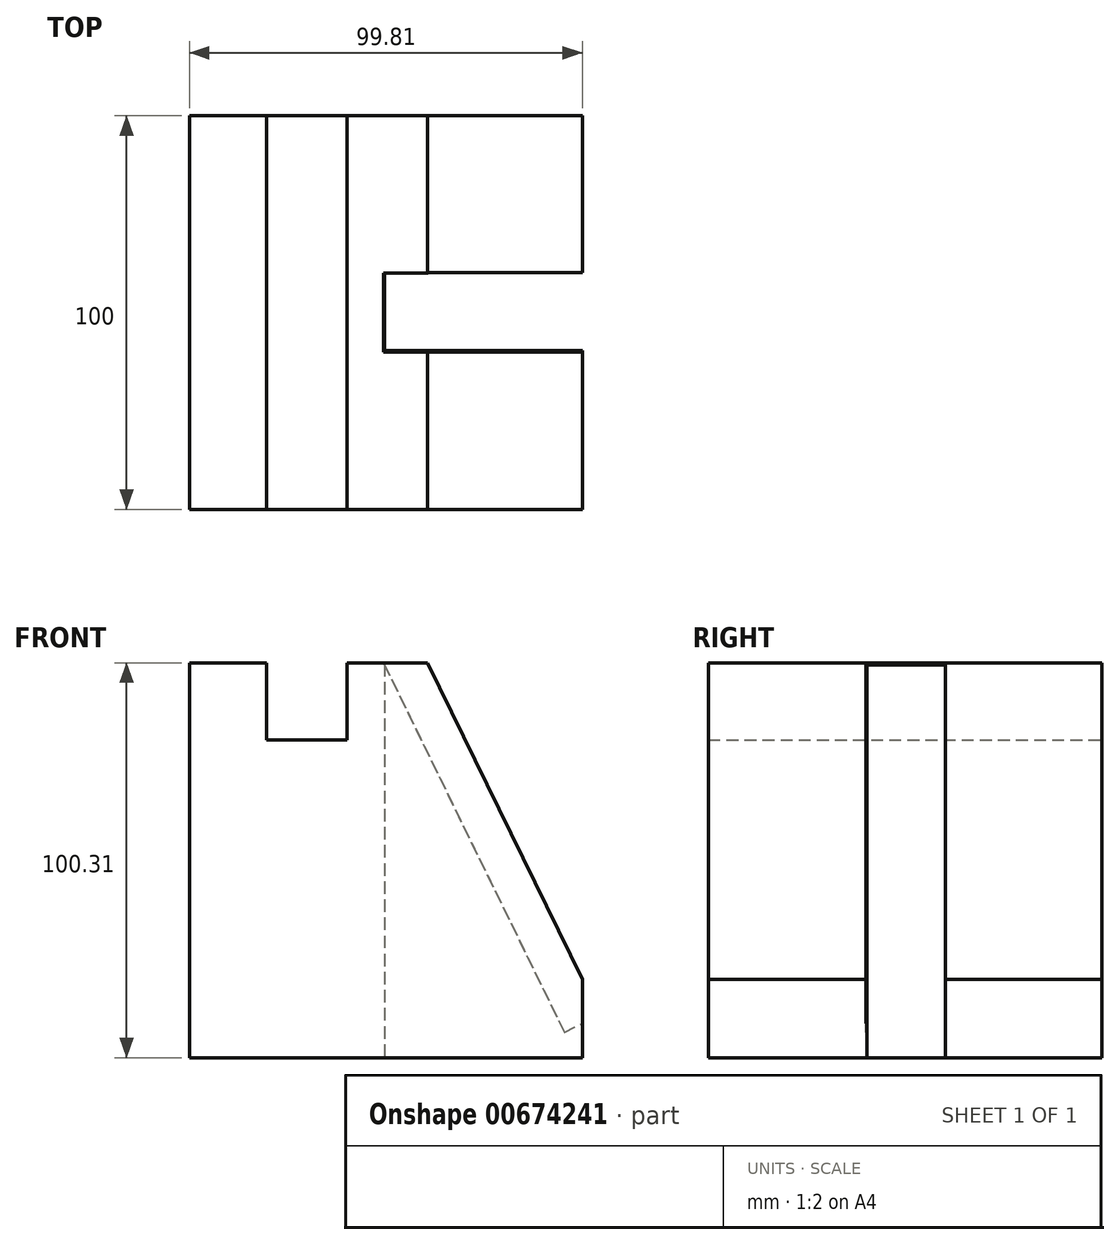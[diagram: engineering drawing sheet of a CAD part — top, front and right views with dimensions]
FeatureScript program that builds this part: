
annotation { "Feature Type Name" : "Feature", "Feature Type Description" : "" }
export const myFeature = defineFeature(function(context is Context, id is Id, definition is map)
    precondition{}
    {
        {
            var Q0;
            Q0=qCreatedBy(makeId("Front.planeOp"),FACE);
            var sketch = newSketch(context, id + "F0", { "sketchPlane" : qUnion([Q0])});
            skLineSegment(sketch, "E0", {"start": v(-74.7, 75.5) * mm, "end": v(-55.16, 75.5) * mm});
            skLineSegment(sketch, "E1", {"start": v(-55.16, 75.5) * mm, "end": v(-55.16, 55.95) * mm});
            skLineSegment(sketch, "E2", {"start": v(-55.16, 55.95) * mm, "end": v(-34.72, 55.95) * mm});
            skLineSegment(sketch, "E3", {"start": v(-34.72, 55.95) * mm, "end": v(-34.72, 75.5) * mm});
            skLineSegment(sketch, "E4", {"start": v(-34.72, 75.5) * mm, "end": v(-14.28, 75.5) * mm});
            skLineSegment(sketch, "E5", {"start": v(-74.7, 75.5) * mm, "end": v(-74.7, -24.82) * mm});
            skLineSegment(sketch, "E6", {"start": v(-74.7, -24.82) * mm, "end": v(25.11, -24.82) * mm});
            skLineSegment(sketch, "E7", {"start": v(25.11, -24.82) * mm, "end": v(25.11, -4.99) * mm});
            skLineSegment(sketch, "E8", {"start": v(25.11, -4.99) * mm, "end": v(-14.28, 75.5) * mm});
            skSolve(sketch);
        }
        {
            var Q0;
            Q0=makeQuery(id+"F0.imprint","IMPRINT",FACE,{"disambiguationData":[TD([[makeQuery(id+"F0.imprint","IMPRINT",EDGE,{"derivedFrom":sQuery(id+"F0.wireOp",EDGE,"E0")}),-1.0]])]});
            extrude(context, id + "F1", {"entities" : qUnion([Q0]), "depth" : 100 * mm, "offsetDistance" : 25 * mm});
        }
        {
            var Q0;
            Q0=makeQuery(id+"F1.opExtrude","SWEPT_FACE",FACE,{"disambiguationData":[OSD([sQuery(id+"F0.wireOp",EDGE,"E8")])]});
            var sketch = newSketch(context, id + "F2", { "sketchPlane" : qUnion([Q0])});
            skLineSegment(sketch, "E9", {"start": v(-100, 74.09) * mm, "end": v(-60, 74.09) * mm});
            skLineSegment(sketch, "E10", {"start": v(-60, 74.09) * mm, "end": v(-40, 74.09) * mm});
            skLineSegment(sketch, "E11", {"start": v(-40, 74.09) * mm, "end": v(0, 74.09) * mm});
            skLineSegment(sketch, "E12", {"start": v(-60, 74.09) * mm, "end": v(-60, -15.52) * mm});
            skLineSegment(sketch, "E13", {"start": v(-60, -15.52) * mm, "end": v(-40, -15.52) * mm});
            skLineSegment(sketch, "E14", {"start": v(-40, -15.52) * mm, "end": v(-40, 74.09) * mm});
            skSolve(sketch);
        }
        {
            var Q0;
            Q0 = qSketchRegion(id + "F2", true);
            extrude(context, id + "F3", {"entities" : qUnion([Q0]), "operationType" : NewBodyOperationType.REMOVE, "oppositeDirection" : true, "depth" : 10 * mm, "offsetDistance" : 25 * mm});
        }
        {
            var Q0;
            Q0=makeQuery(id+"F3.boolean.opBoolean","COPY",FACE,{"derivedFrom":makeQuery(id+"F3.opExtrude","SWEPT_FACE",FACE,{"disambiguationData":[OSD([sQuery(id+"F2.wireOp",EDGE,"E10")])]})});
            extrude(context, id + "F4", {"entities" : qUnion([Q0]), "operationType" : NewBodyOperationType.REMOVE, "oppositeDirection" : true, "depth" : 10 * mm, "offsetDistance" : 25 * mm});
        }
        {
            var Q0;
            Q0=makeQuery(id+"F3.boolean.opBoolean","COPY",FACE,{"derivedFrom":makeQuery(id+"F3.opExtrude","SWEPT_FACE",FACE,{"disambiguationData":[OSD([sQuery(id+"F2.wireOp",EDGE,"E13")])]})});
            extrude(context, id + "F5", {"entities" : qUnion([Q0]), "operationType" : NewBodyOperationType.REMOVE, "oppositeDirection" : true, "depth" : 10 * mm, "offsetDistance" : 25 * mm});
        }
        {
            var Q0;
            Q0=makeQuery(id+"F1.opExtrude","SWEPT_FACE",FACE,{"disambiguationData":[OSD([sQuery(id+"F0.wireOp",EDGE,"E6")])]});
            var sketch = newSketch(context, id + "F6", { "sketchPlane" : qUnion([Q0])});
            skLineSegment(sketch, "E15", {"start": v(25.11, 100) * mm, "end": v(25.11, 59.66) * mm});
            skLineSegment(sketch, "E16", {"start": v(25.11, 0) * mm, "end": v(25.11, 39.82) * mm});
            skLineSegment(sketch, "E17", {"start": v(25.11, 59.66) * mm, "end": v(-25.18, 59.66) * mm});
            skLineSegment(sketch, "E18", {"start": v(25.11, 39.82) * mm, "end": v(-25.18, 39.82) * mm});
            skLineSegment(sketch, "E19", {"start": v(-25.18, 39.82) * mm, "end": v(-25.18, 59.66) * mm});
            skSolve(sketch);
        }
        {
            var Q0;
            {var subQ0=sQuery(id+"F6.wireOp",EDGE,"E17");Q0=makeQuery(id+"F6.imprint","IMPRINT",FACE,{"disambiguationData":[TD([[makeQuery(id+"F6.imprint","IMPRINT",EDGE,{"derivedFrom":subQ0}),1.0]])]});}
            extrude(context, id + "F7", {"entities" : qUnion([Q0]), "operationType" : NewBodyOperationType.REMOVE, "oppositeDirection" : true, "depth" : 100 * mm, "offsetDistance" : 25 * mm});
        }
    });
